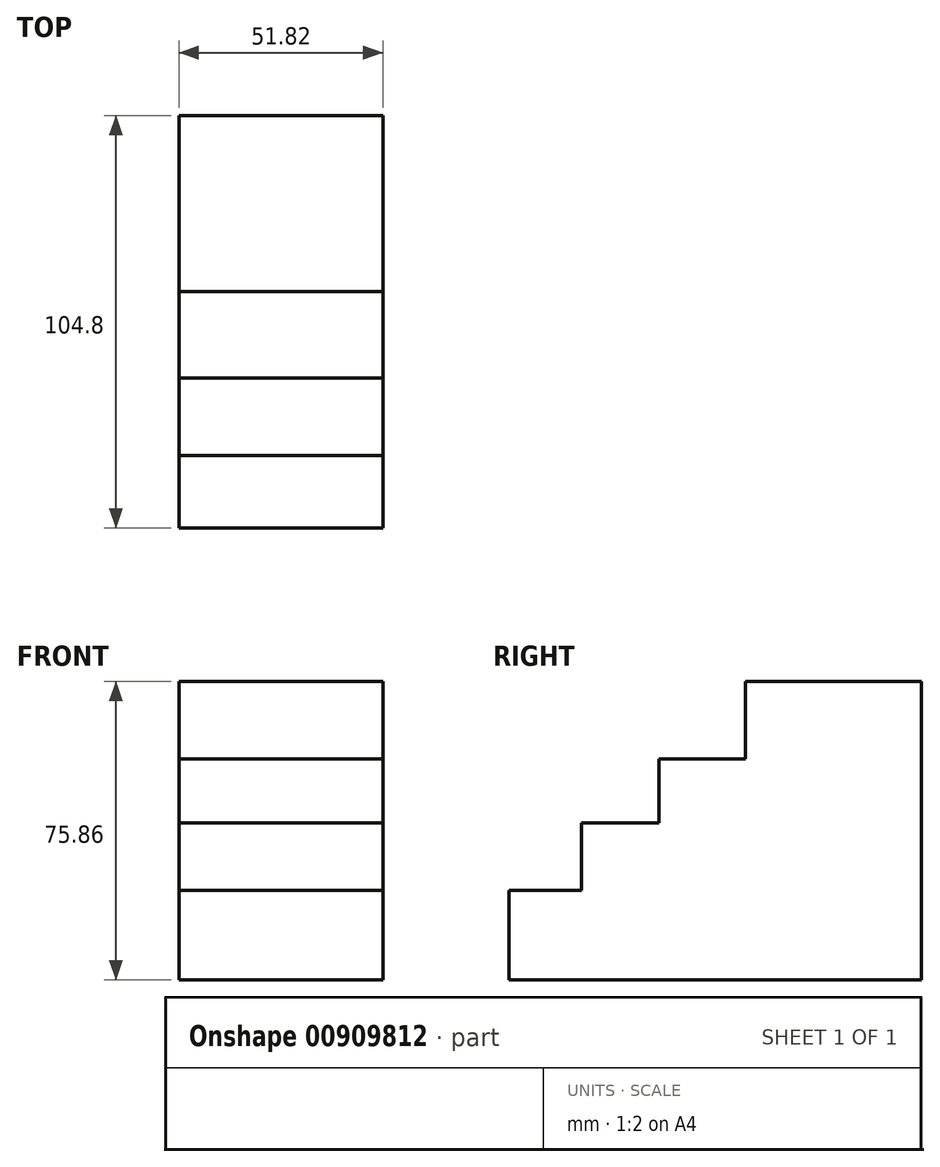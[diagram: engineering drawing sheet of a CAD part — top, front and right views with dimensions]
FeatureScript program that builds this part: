
annotation { "Feature Type Name" : "Feature", "Feature Type Description" : "" }
export const myFeature = defineFeature(function(context is Context, id is Id, definition is map)
    precondition{}
    {
        {
            var Q0;
            Q0=qCreatedBy(makeId("Right.planeOp"),FACE);
            var sketch = newSketch(context, id + "F0", { "sketchPlane" : qUnion([Q0])});
            skLineSegment(sketch, "E0.bottom", {"start": v(42.63, 41.85) * mm, "end": v(-2.1, 41.85) * mm});
            skLineSegment(sketch, "E0.top", {"start": v(42.63, -34) * mm, "end": v(-2.1, -34) * mm});
            skLineSegment(sketch, "E0.left", {"start": v(42.63, 41.85) * mm, "end": v(42.63, -34) * mm});
            skLineSegment(sketch, "E0.right", {"start": v(-2.1, 41.85) * mm, "end": v(-2.1, -34) * mm});
            skLineSegment(sketch, "E1.bottom", {"start": v(-2.1, 22.12) * mm, "end": v(-24.02, 22.12) * mm});
            skLineSegment(sketch, "E1.top", {"start": v(-2.1, -34) * mm, "end": v(-24.02, -34) * mm});
            skLineSegment(sketch, "E1.left", {"start": v(-2.1, 22.12) * mm, "end": v(-2.1, -34) * mm});
            skLineSegment(sketch, "E1.right", {"start": v(-24.02, 22.12) * mm, "end": v(-24.02, -34) * mm});
            skLineSegment(sketch, "E2.bottom", {"start": v(-24.02, -34) * mm, "end": v(-43.75, -34) * mm});
            skLineSegment(sketch, "E2.top", {"start": v(-24.02, 5.9) * mm, "end": v(-43.75, 5.9) * mm});
            skLineSegment(sketch, "E2.left", {"start": v(-24.02, -34) * mm, "end": v(-24.02, 5.9) * mm});
            skLineSegment(sketch, "E2.right", {"start": v(-43.75, -34) * mm, "end": v(-43.75, 5.9) * mm});
            skLineSegment(sketch, "E3.bottom", {"start": v(-43.75, -34) * mm, "end": v(-62.17, -34) * mm});
            skLineSegment(sketch, "E3.top", {"start": v(-43.75, -11.2) * mm, "end": v(-62.17, -11.2) * mm});
            skLineSegment(sketch, "E3.left", {"start": v(-43.75, -34) * mm, "end": v(-43.75, -11.2) * mm});
            skLineSegment(sketch, "E3.right", {"start": v(-62.17, -34) * mm, "end": v(-62.17, -11.2) * mm});
            skSolve(sketch);
        }
        {
            var Q0;
            Q0 = qSketchRegion(id + "F0", true);
            extrude(context, id + "F1", {"entities" : qUnion([Q0]), "depth" : 51.82 * mm, "offsetDistance" : 25.4 * mm});
        }
    });
